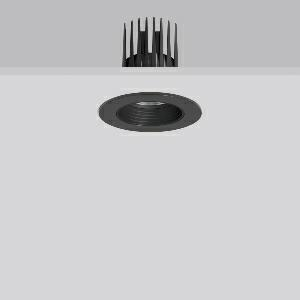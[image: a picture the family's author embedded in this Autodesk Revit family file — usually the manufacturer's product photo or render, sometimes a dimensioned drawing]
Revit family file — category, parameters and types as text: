
# Revit family: heledon_mini_e_901746_003_8354
name_source: partatom
category: Lighting Fixtures
units: mm (PartAtom-declared; Revit-internal decimal feet)

## family parameters
Cut with Voids When Loaded = No
Host = Face
Light Source = No
Part Type = Normal
Room Calculation Point = No
Round Connector Dimension = Use Diameter
Shared = No

## types (1)
- HELEDON mini E (1 x LED Modul 930, 2250 lm, 3000)
    Apparent Load = 20 VA
    Approval mark = CE
    CIE Flux Codes = 80 99 100 100 100
    Color Rendering = 90
    Color Temperature = 3000
    Default Elevation = 1800 mm
    Description = Series: HELEDON mini
Round recessed downlight. Housing: die-cast aluminium, powder-coated. Black plastic ring and recessed LED to prevent glare from the side. Optical assembly with lens made of plastic (polycarbonate) for the best homogeneous light distribution - can be changed without tools. Best colour rendering index Ra>90. Suitable for Recessed ceiling mounting. Installation without tools thanks to spring fastening system. Including separate LED converter with connecting cable 600 mm.High quality converter without flickering and stroboscopic effect. Through-wiring box (5 pole) available as accessory. The following accessories can be mounted without use of tools: interchangeable lenses, decorative glasses, honeycomb louvre, clear and frosted diffusers, white interchangeable plastic ring. 
Colour: deep black, matt (RAL 9005)
Diameter: 124 mm
Height: 3 mm
Cut-out diameter: 114 mm
Recess height: 170 mm
Luminaire: recess height: 120 mm
Lamp: LED
Socket: without socket
Colour temperature: 3000K
Colour rendering index (CRI): 92
System power: 20 W
Rated luminous flux: 2250 lm
Luminous efficiency: 113 lm/W
Control gear: Regulated power supply
Protection class: II
Type of protection: IP 20
    Height = 0 mm  [stored 0 ft]
    Lamp = 1 x LED Modul 930
    Lamp Light Flux = 2250 lm
    Lamp count = 1
    Length = 124 mm  [stored 0.406824 ft]
    Lifetime = 50000 h
    Luminous efficacy = 113 lm/W
    Manufacturer = RZB
    ModVariant = No
    Model = 901746.003
    Mounting Place = Ceiling
    Mounting Type = Recessed
    Number of Poles = 1
    OnlyDefault = Yes
    Power Factor = 1
    Product Name = HELEDON mini E
    Product group = Recessed downlights
    ProductGroupID = 402
    Protection Class = Protection class II
    Protection Degree = IP 20
    RLX_Detail_Level = 1
    RLX_Emergency_Light_Flux = 0 lm
    RLX_Emergency_Type = 0
    RLX_Emergency_Type_DB = No
    RlxData = <blob elided: 126933 chars, md5=4b1e36d0>
    Socket = socket
    Standby Power = 0 W
    System Light Flux = 2250 lm
    System Power = 20 W
    Type Comments = Product without accessories
    Type Image = 901656.003.jpg
    URL = http://relux.com
    VarID = ---
    Voltage = 230 V
    Voltage Range = 220-240 V
    Weight = 0.00 kg
    Width = 0 mm  [stored 0 ft]

note: [stored X ft] marks values corroborated as IEEE doubles in the binary element streams (Revit-internal decimal feet)

## geometry (parser evidence)
native form markers: Blend x4, Sweep x11
no freeform markers — native parametric forms only
